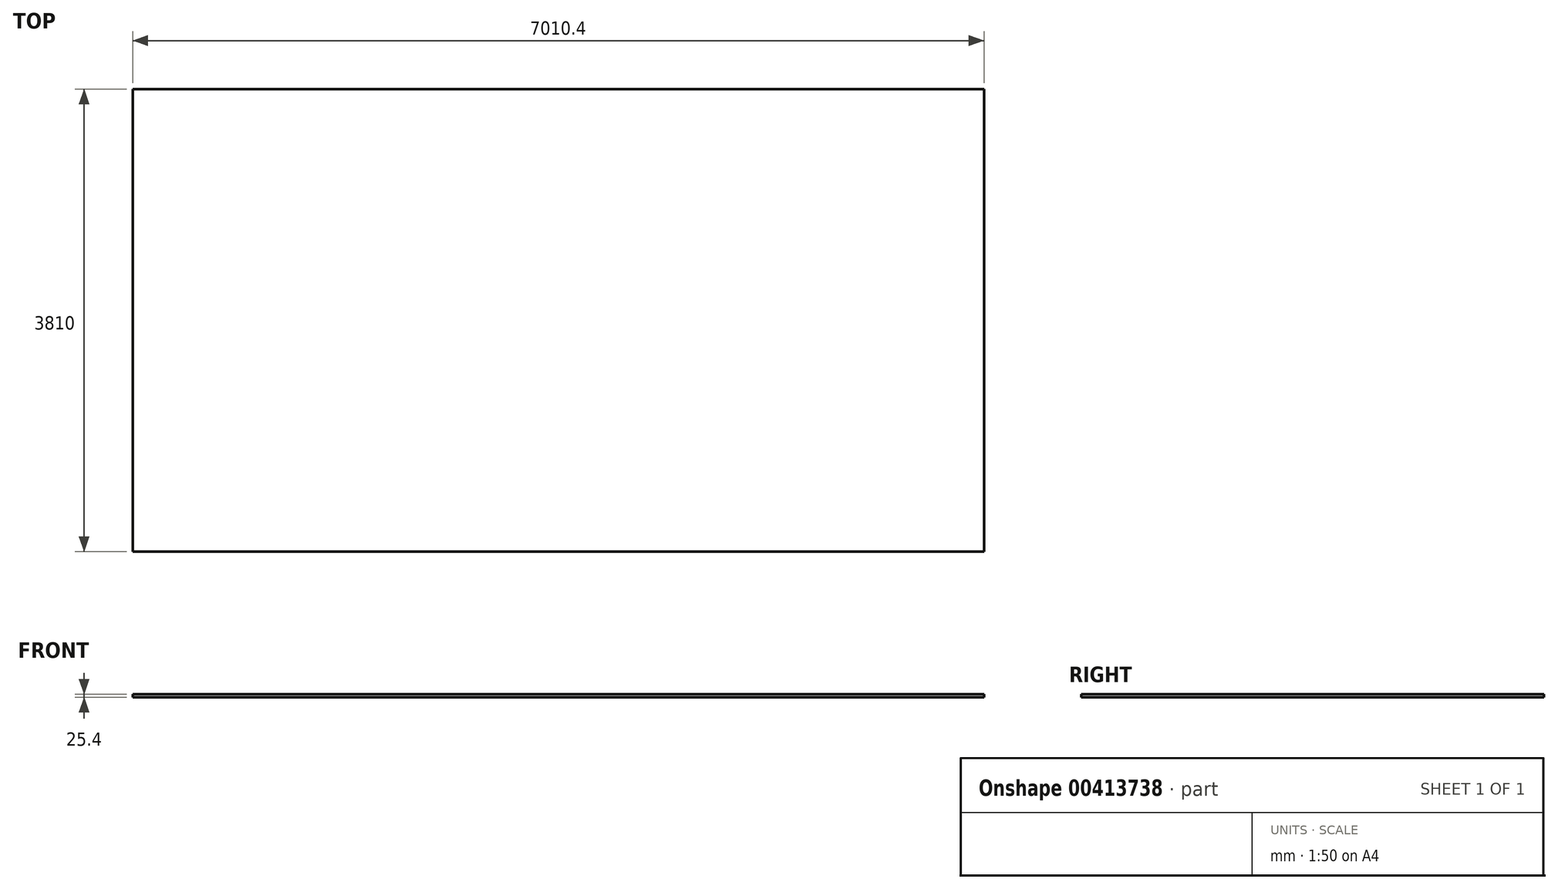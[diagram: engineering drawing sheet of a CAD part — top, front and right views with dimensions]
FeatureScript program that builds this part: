
annotation { "Feature Type Name" : "Feature", "Feature Type Description" : "" }
export const myFeature = defineFeature(function(context is Context, id is Id, definition is map)
    precondition{}
    {
        {
            var Q0;
            Q0=qCreatedBy(makeId("Top.planeOp"),FACE);
            var sketch = newSketch(context, id + "F0", { "sketchPlane" : qUnion([Q0])});
            skLineSegment(sketch, "E0.bottom", {"start": v(-3505.2, 1905) * mm, "end": v(3505.2, 1905) * mm});
            skLineSegment(sketch, "E0.top", {"start": v(-3505.2, -1905) * mm, "end": v(3505.2, -1905) * mm});
            skLineSegment(sketch, "E0.left", {"start": v(-3505.2, 1905) * mm, "end": v(-3505.2, -1905) * mm});
            skLineSegment(sketch, "E0.right", {"start": v(3505.2, 1905) * mm, "end": v(3505.2, -1905) * mm});
            skPoint(sketch, "E0.middle", {"position": v(0, 0) * mm});
            skSolve(sketch);
        }
        {
            var Q0;
            Q0=makeQuery(id+"F0.imprint","IMPRINT",FACE,{"disambiguationData":[TD([[makeQuery(id+"F0.imprint","IMPRINT",EDGE,{"derivedFrom":sQuery(id+"F0.wireOp",EDGE,"E0.bottom")}),-1.0]])]});
            extrude(context, id + "F1", {"entities" : qUnion([Q0]), "endBound" : BoundingType.SYMMETRIC, "depth" : 25.4 * mm});
        }
    });
